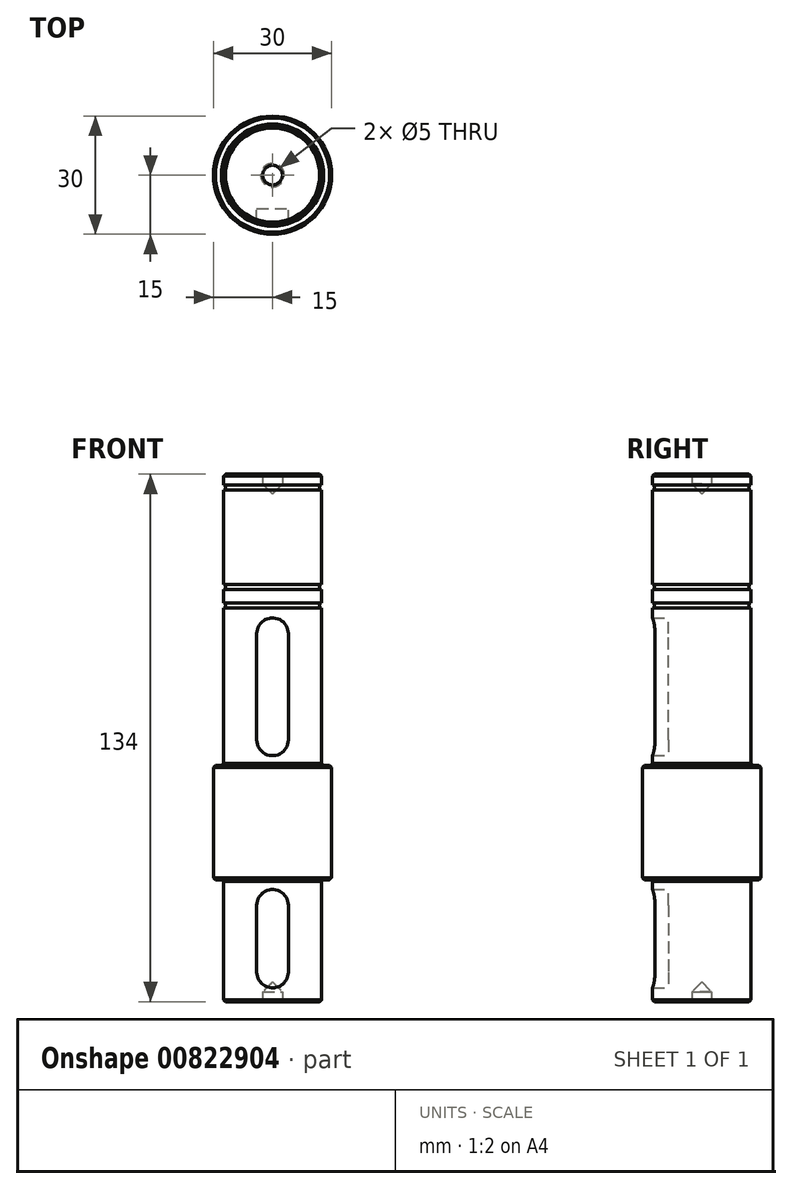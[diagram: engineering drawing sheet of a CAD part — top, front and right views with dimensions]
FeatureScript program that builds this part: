
annotation { "Feature Type Name" : "Feature", "Feature Type Description" : "" }
export const myFeature = defineFeature(function(context is Context, id is Id, definition is map)
    precondition{}
    {
        {
            var Q0;
            Q0=qCreatedBy(makeId("Front.planeOp"),FACE);
            var sketch = newSketch(context, id + "F0", { "sketchPlane" : qUnion([Q0])});
            skLineSegment(sketch, "E0", {"start": v(0, 0) * mm, "end": v(0, 23) * mm});
            skLineSegment(sketch, "E1", {"start": v(0, 23) * mm, "end": v(2.5, 25.5) * mm});
            skLineSegment(sketch, "E2", {"start": v(2.5, 25.5) * mm, "end": v(2.5, 28) * mm});
            skLineSegment(sketch, "E3", {"start": v(2.5, 28) * mm, "end": v(12.47, 28) * mm});
            skLineSegment(sketch, "E4", {"start": v(12.47, 28) * mm, "end": v(12.47, 25.3) * mm});
            skLineSegment(sketch, "E5", {"start": v(12.47, 25.3) * mm, "end": v(11.95, 25.3) * mm});
            skLineSegment(sketch, "E6", {"start": v(11.95, 25.3) * mm, "end": v(11.95, 24) * mm});
            skLineSegment(sketch, "E7", {"start": v(11.95, 24) * mm, "end": v(12.5, 24) * mm});
            skLineSegment(sketch, "E8", {"start": v(12.5, 24) * mm, "end": v(12.5, 0) * mm});
            skLineSegment(sketch, "E9", {"start": v(12.5, 0) * mm, "end": v(12.5, 0) * mm});
            skLineSegment(sketch, "E10", {"start": v(12.5, -1.3) * mm, "end": v(12.5, -4.7) * mm});
            skLineSegment(sketch, "E11", {"start": v(15, -51) * mm, "end": v(15, -75) * mm});
            skLineSegment(sketch, "E12", {"start": v(15, -75) * mm, "end": v(12.5, -75) * mm});
            skLineSegment(sketch, "E13", {"start": v(12.5, -75) * mm, "end": v(12.5, -105) * mm});
            skLineSegment(sketch, "E14", {"start": v(12.5, -105) * mm, "end": v(11.95, -105) * mm, "construction": true});
            skLineSegment(sketch, "E15", {"start": v(11.95, -105) * mm, "end": v(11.95, -106.3) * mm, "construction": true});
            skLineSegment(sketch, "E16", {"start": v(11.95, -106.3) * mm, "end": v(12.5, -106.3) * mm, "construction": true});
            skLineSegment(sketch, "E17", {"start": v(12.5, -106) * mm, "end": v(2.5, -106) * mm});
            skLineSegment(sketch, "E18", {"start": v(2.5, -106) * mm, "end": v(2.5, -103.5) * mm});
            skLineSegment(sketch, "E19", {"start": v(2.5, -103.5) * mm, "end": v(0, -101) * mm});
            skLineSegment(sketch, "E20", {"start": v(0, -101) * mm, "end": v(0, 0) * mm});
            skLineSegment(sketch, "E21", {"start": v(15, -51) * mm, "end": v(15, -51) * mm});
            skLineSegment(sketch, "E22", {"start": v(15, -51) * mm, "end": v(15, -46) * mm});
            skLineSegment(sketch, "E23", {"start": v(15, -46) * mm, "end": v(12.5, -46) * mm});
            skLineSegment(sketch, "E24", {"start": v(12.5, -4.7) * mm, "end": v(11.95, -4.7) * mm});
            skLineSegment(sketch, "E25", {"start": v(11.95, -4.7) * mm, "end": v(11.95, -6) * mm});
            skLineSegment(sketch, "E26", {"start": v(11.95, -6) * mm, "end": v(12.5, -6) * mm});
            skLineSegment(sketch, "E27.trimOffspring", {"start": v(12.5, -6) * mm, "end": v(12.5, -46) * mm});
            skLineSegment(sketch, "E28", {"start": v(12.5, 0) * mm, "end": v(11.95, 0) * mm});
            skLineSegment(sketch, "E29", {"start": v(11.95, 0) * mm, "end": v(11.95, -1.3) * mm});
            skLineSegment(sketch, "E30", {"start": v(11.95, -1.3) * mm, "end": v(12.5, -1.3) * mm});
            skLineSegment(sketch, "E31", {"start": v(12.5, -105) * mm, "end": v(12.5, -106) * mm});
            skSolve(sketch);
        }
        {
            var Q0;
            Q0 = qSketchRegion(id + "F0", true);
            var Q1;
            Q1=sQuery(id+"F0.wireOp",EDGE,"E20");
            revolve(context, id + "F1", {"surfaceOperationType" : NewSurfaceOperationType.NEW, "entities" : qUnion([Q0]), "axis" : qUnion([Q1]), "revolveType" : RevolveType.FULL});
        }
        {
            var Q0;
            Q0=makeQuery(id+"F1.opRevolve","SWEPT_FACE",FACE,{"disambiguationData":[OSD([sQuery(id+"F0.wireOp",EDGE,"E23")])]});
            var Q1;
            Q1=makeQuery(id+"F1.opRevolve","SWEPT_FACE",FACE,{"disambiguationData":[OSD([sQuery(id+"F0.wireOp",EDGE,"E12")])]});
            var Q2;
            Q2=makeQuery(id+"F1.opRevolve","SWEPT_EDGE",EDGE,{"disambiguationData":[OSD([sQuery(id+"F0.wireOp",EDGE,"iQIRzjXh-yBdl-OMpJ-ZXXb-tQpLsTRLM0CL"),sQuery(id+"F0.wireOp",EDGE,"E17")])]});
            var Q3;
            Q3=makeQuery(id+"F1.opRevolve","SWEPT_EDGE",EDGE,{"disambiguationData":[OSD([sQuery(id+"F0.wireOp",EDGE,"E3"),sQuery(id+"F0.wireOp",EDGE,"E4")])]});
            chamfer(context, id + "F2", {"entities" : qUnion([Q0, Q1, Q2, Q3]), "width" : 0.5 * mm, "tangentPropagation" : true});
        }
        {
            var Q0;
            Q0=qCreatedBy(makeId("Front.planeOp"),FACE);
            cPlane(context, id + "F3", {"entities" : qUnion([Q0]), "cplaneType" : CPlaneType.OFFSET, "offset" : 8.5 * mm, "width" : 150 * mm, "height" : 150 * mm});
        }
        {
            var Q0;
            Q0=qCreatedBy(id+"F3.planeOp",FACE);
            var sketch = newSketch(context, id + "F4", { "sketchPlane" : qUnion([Q0])});
            skLineSegment(sketch, "E32", {"start": v(0, 0) * mm, "end": v(0, -75.98) * mm, "construction": true});
            skLineSegment(sketch, "E33.bottom", {"start": v(4, -39.5) * mm, "end": v(-4, -39.5) * mm, "construction": true});
            skLineSegment(sketch, "E33.top", {"start": v(4, -12.5) * mm, "end": v(-4, -12.5) * mm, "construction": true});
            skLineSegment(sketch, "E33.left", {"start": v(4, -39.5) * mm, "end": v(4, -12.5) * mm});
            skLineSegment(sketch, "E33.right", {"start": v(-4, -39.5) * mm, "end": v(-4, -12.5) * mm});
            skPoint(sketch, "E33.middle", {"position": v(0, -26) * mm});
            skLineSegment(sketch, "E34.bottom", {"start": v(4, -81.5) * mm, "end": v(-4, -81.5) * mm, "construction": true});
            skLineSegment(sketch, "E34.top", {"start": v(4, -98.5) * mm, "end": v(-4, -98.5) * mm, "construction": true});
            skLineSegment(sketch, "E34.left", {"start": v(4, -81.5) * mm, "end": v(4, -98.5) * mm});
            skLineSegment(sketch, "E34.right", {"start": v(-4, -81.5) * mm, "end": v(-4, -98.5) * mm});
            skPoint(sketch, "E34.middle", {"position": v(0, -90) * mm});
            skArc(sketch, "E35", {"start": v(4, -81.5) * mm, "mid": v(0, -77.5) * mm, "end": v(-4, -81.5) * mm});
            skArc(sketch, "E36", {"start": v(-4, -98.5) * mm, "mid": v(0, -102.5) * mm, "end": v(4, -98.5) * mm});
            skArc(sketch, "E37", {"start": v(-4, -39.5) * mm, "mid": v(0, -43.5) * mm, "end": v(4, -39.5) * mm});
            skArc(sketch, "E38", {"start": v(4, -12.5) * mm, "mid": v(0, -8.5) * mm, "end": v(-4, -12.5) * mm});
            skSolve(sketch);
        }
        {
            var Q0;
            Q0 = qSketchRegion(id + "F4", true);
            extrude(context, id + "F5", {"entities" : qUnion([Q0]), "operationType" : NewBodyOperationType.REMOVE, "depth" : 25 * mm, "offsetDistance" : 25 * mm});
        }
    });
